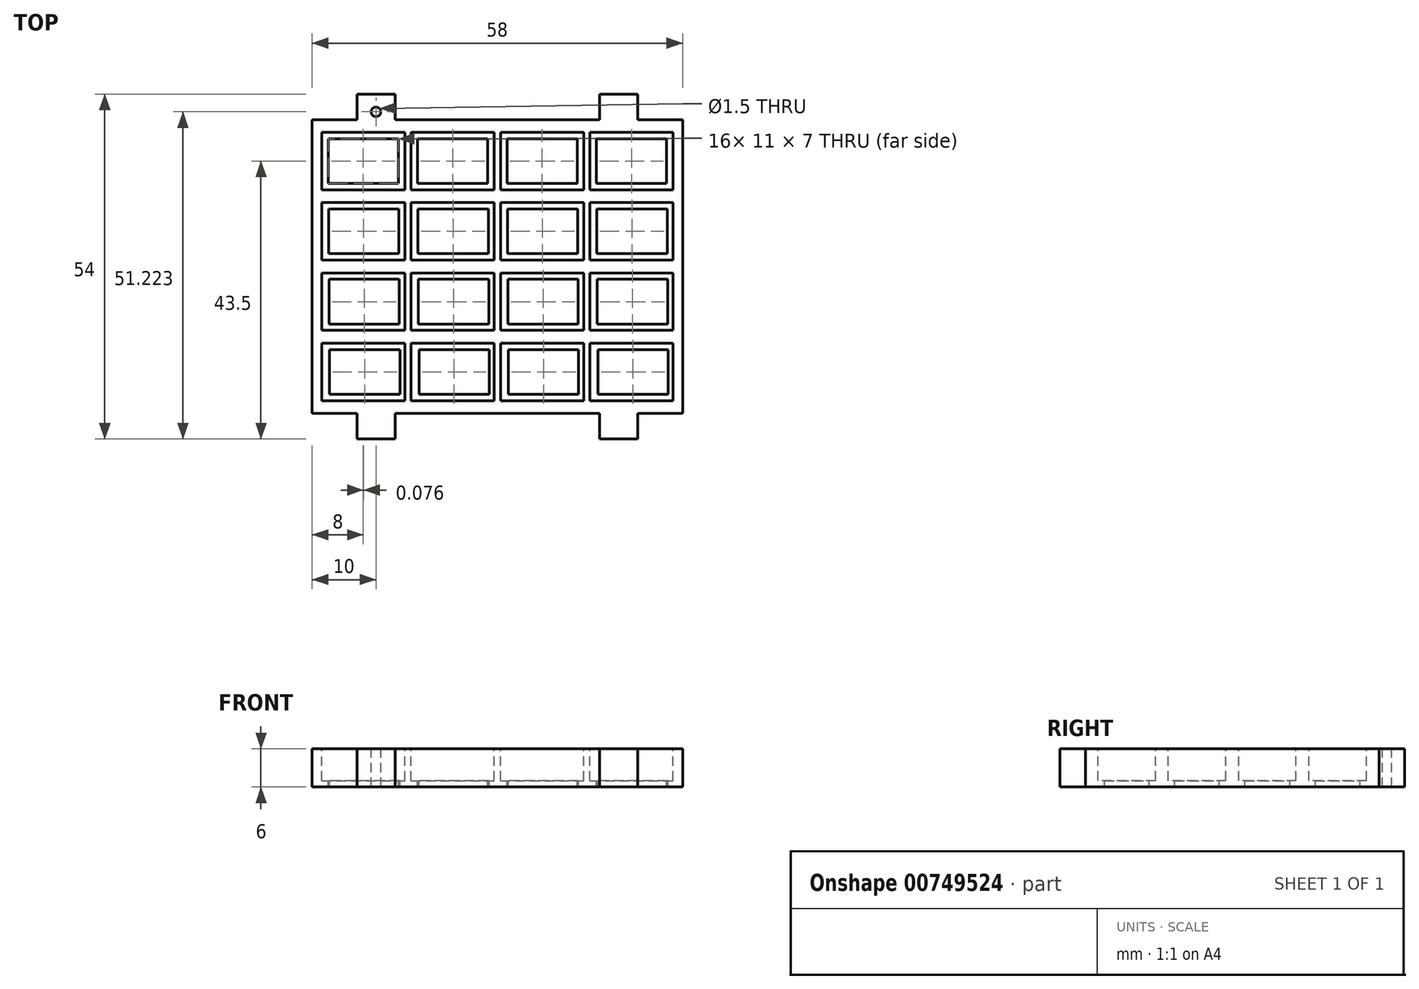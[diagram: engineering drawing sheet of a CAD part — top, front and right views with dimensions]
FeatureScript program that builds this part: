
annotation { "Feature Type Name" : "Feature", "Feature Type Description" : "" }
export const myFeature = defineFeature(function(context is Context, id is Id, definition is map)
    precondition{}
    {
        {
            var Q0;
            Q0=qCreatedBy(makeId("Top.planeOp"),FACE);
            var sketch = newSketch(context, id + "F0", { "sketchPlane" : qUnion([Q0])});
            skLineSegment(sketch, "E0.bottom", {"start": v(-29, 23) * mm, "end": v(29, 23) * mm});
            skLineSegment(sketch, "E0.top", {"start": v(-29, -23) * mm, "end": v(29, -23) * mm});
            skLineSegment(sketch, "E0.left", {"start": v(-29, 23) * mm, "end": v(-29, -23) * mm});
            skLineSegment(sketch, "E0.right", {"start": v(29, 23) * mm, "end": v(29, -23) * mm});
            skSolve(sketch);
        }
        {
            var Q0;
            Q0=makeQuery(id+"F0.imprint","IMPRINT",FACE,{"disambiguationData":[TD([[makeQuery(id+"F0.imprint","IMPRINT",EDGE,{"derivedFrom":sQuery(id+"F0.wireOp",EDGE,"E0.bottom")}),-1.0]])]});
            extrude(context, id + "F1", {"entities" : qUnion([Q0]), "depth" : 6 * mm, "offsetDistance" : 25 * mm});
        }
        {
            var Q0;
            Q0=makeQuery(id+"F1.opExtrude","CAP_FACE",FACE,{"disambiguationData":[OSD([sQuery(id+"F0.wireOp",EDGE,"E0.bottom"),sQuery(id+"F0.wireOp",EDGE,"E0.top"),sQuery(id+"F0.wireOp",EDGE,"E0.left"),sQuery(id+"F0.wireOp",EDGE,"E0.right")])],"isStart":false});
            var sketch = newSketch(context, id + "F2", { "sketchPlane" : qUnion([Q0])});
            skPoint(sketch, "E1.middle", {"position": v(0, 0) * mm});
            skLineSegment(sketch, "E2.bottom", {"start": v(-15.5, 13) * mm, "end": v(-26.5, 13) * mm});
            skLineSegment(sketch, "E2.top", {"start": v(-15.5, 20) * mm, "end": v(-26.5, 20) * mm});
            skLineSegment(sketch, "E2.left", {"start": v(-15.5, 13) * mm, "end": v(-15.5, 20) * mm});
            skLineSegment(sketch, "E2.right", {"start": v(-26.5, 13) * mm, "end": v(-26.5, 20) * mm});
            skPoint(sketch, "E2.middle", {"position": v(-21, 16.5) * mm});
            skLineSegment(sketch, "E3.1.0.0", {"start": v(-12.5, 13) * mm, "end": v(-12.5, 20) * mm});
            skLineSegment(sketch, "E3.1.0.1", {"start": v(-1.5, 13) * mm, "end": v(-1.5, 20) * mm});
            skLineSegment(sketch, "E3.1.0.2", {"start": v(-1.5, 20) * mm, "end": v(-12.5, 20) * mm});
            skPoint(sketch, "E3.1.0.3", {"position": v(-7, 16.5) * mm});
            skLineSegment(sketch, "E3.1.0.4", {"start": v(-1.5, 13) * mm, "end": v(-12.5, 13) * mm});
            skLineSegment(sketch, "E3.2.0.0", {"start": v(1.5, 13) * mm, "end": v(1.5, 20) * mm});
            skLineSegment(sketch, "E3.2.0.1", {"start": v(12.5, 13) * mm, "end": v(12.5, 20) * mm});
            skLineSegment(sketch, "E3.2.0.2", {"start": v(12.5, 20) * mm, "end": v(1.5, 20) * mm});
            skPoint(sketch, "E3.2.0.3", {"position": v(7, 16.5) * mm});
            skLineSegment(sketch, "E3.2.0.4", {"start": v(12.5, 13) * mm, "end": v(1.5, 13) * mm});
            skLineSegment(sketch, "E3.3.0.0", {"start": v(15.5, 13) * mm, "end": v(15.5, 20) * mm});
            skLineSegment(sketch, "E3.3.0.1", {"start": v(26.5, 13) * mm, "end": v(26.5, 20) * mm});
            skLineSegment(sketch, "E3.3.0.2", {"start": v(26.5, 20) * mm, "end": v(15.5, 20) * mm});
            skPoint(sketch, "E3.3.0.3", {"position": v(21, 16.5) * mm});
            skLineSegment(sketch, "E3.3.0.4", {"start": v(26.5, 13) * mm, "end": v(15.5, 13) * mm});
            skLineSegment(sketch, "E3.direction1", {"start": v(-26.5, 13) * mm, "end": v(-12.5, 13) * mm, "construction": true});
            skLineSegment(sketch, "E4.1.0.0", {"start": v(15.58, 2) * mm, "end": v(15.58, 9) * mm});
            skLineSegment(sketch, "E4.1.0.1", {"start": v(26.58, 9) * mm, "end": v(15.58, 9) * mm});
            skLineSegment(sketch, "E4.1.0.2", {"start": v(-26.42, 2) * mm, "end": v(-12.42, 2) * mm, "construction": true});
            skPoint(sketch, "E4.1.0.3", {"position": v(-20.92, 5.5) * mm});
            skLineSegment(sketch, "E4.1.0.4", {"start": v(1.58, 2) * mm, "end": v(1.58, 9) * mm});
            skLineSegment(sketch, "E4.1.0.5", {"start": v(-1.42, 2) * mm, "end": v(-12.42, 2) * mm});
            skLineSegment(sketch, "E4.1.0.6", {"start": v(-1.42, 9) * mm, "end": v(-12.42, 9) * mm});
            skLineSegment(sketch, "E4.1.0.7", {"start": v(-1.42, 2) * mm, "end": v(-1.42, 9) * mm});
            skLineSegment(sketch, "E4.1.0.8", {"start": v(-12.42, 2) * mm, "end": v(-12.42, 9) * mm});
            skLineSegment(sketch, "E4.1.0.9", {"start": v(-26.42, 2) * mm, "end": v(-26.42, 9) * mm});
            skLineSegment(sketch, "E4.1.0.10", {"start": v(-15.42, 2) * mm, "end": v(-15.42, 9) * mm});
            skLineSegment(sketch, "E4.1.0.11", {"start": v(-15.42, 9) * mm, "end": v(-26.42, 9) * mm});
            skPoint(sketch, "E4.1.0.12", {"position": v(7.08, 5.5) * mm});
            skLineSegment(sketch, "E4.1.0.13", {"start": v(12.58, 2) * mm, "end": v(1.58, 2) * mm});
            skLineSegment(sketch, "E4.1.0.14", {"start": v(12.58, 9) * mm, "end": v(1.58, 9) * mm});
            skLineSegment(sketch, "E4.1.0.15", {"start": v(12.58, 2) * mm, "end": v(12.58, 9) * mm});
            skLineSegment(sketch, "E4.1.0.16", {"start": v(26.58, 2) * mm, "end": v(26.58, 9) * mm});
            skLineSegment(sketch, "E4.1.0.17", {"start": v(26.58, 2) * mm, "end": v(15.58, 2) * mm});
            skPoint(sketch, "E4.1.0.18", {"position": v(-6.92, 5.5) * mm});
            skPoint(sketch, "E4.1.0.19", {"position": v(21.08, 5.5) * mm});
            skLineSegment(sketch, "E4.1.0.20", {"start": v(-15.42, 2) * mm, "end": v(-26.42, 2) * mm});
            skLineSegment(sketch, "E4.2.0.0", {"start": v(15.65, -9) * mm, "end": v(15.65, -2) * mm});
            skLineSegment(sketch, "E4.2.0.1", {"start": v(26.65, -2) * mm, "end": v(15.65, -2) * mm});
            skLineSegment(sketch, "E4.2.0.2", {"start": v(-26.35, -9) * mm, "end": v(-12.35, -9) * mm, "construction": true});
            skPoint(sketch, "E4.2.0.3", {"position": v(-20.85, -5.5) * mm});
            skLineSegment(sketch, "E4.2.0.4", {"start": v(1.65, -9) * mm, "end": v(1.65, -2) * mm});
            skLineSegment(sketch, "E4.2.0.5", {"start": v(-1.35, -9) * mm, "end": v(-12.35, -9) * mm});
            skLineSegment(sketch, "E4.2.0.6", {"start": v(-1.35, -2) * mm, "end": v(-12.35, -2) * mm});
            skLineSegment(sketch, "E4.2.0.7", {"start": v(-1.35, -9) * mm, "end": v(-1.35, -2) * mm});
            skLineSegment(sketch, "E4.2.0.8", {"start": v(-12.35, -9) * mm, "end": v(-12.35, -2) * mm});
            skLineSegment(sketch, "E4.2.0.9", {"start": v(-26.35, -9) * mm, "end": v(-26.35, -2) * mm});
            skLineSegment(sketch, "E4.2.0.10", {"start": v(-15.35, -9) * mm, "end": v(-15.35, -2) * mm});
            skLineSegment(sketch, "E4.2.0.11", {"start": v(-15.35, -2) * mm, "end": v(-26.35, -2) * mm});
            skPoint(sketch, "E4.2.0.12", {"position": v(7.15, -5.5) * mm});
            skLineSegment(sketch, "E4.2.0.13", {"start": v(12.65, -9) * mm, "end": v(1.65, -9) * mm});
            skLineSegment(sketch, "E4.2.0.14", {"start": v(12.65, -2) * mm, "end": v(1.65, -2) * mm});
            skLineSegment(sketch, "E4.2.0.15", {"start": v(12.65, -9) * mm, "end": v(12.65, -2) * mm});
            skLineSegment(sketch, "E4.2.0.16", {"start": v(26.65, -9) * mm, "end": v(26.65, -2) * mm});
            skLineSegment(sketch, "E4.2.0.17", {"start": v(26.65, -9) * mm, "end": v(15.65, -9) * mm});
            skPoint(sketch, "E4.2.0.18", {"position": v(-6.85, -5.5) * mm});
            skPoint(sketch, "E4.2.0.19", {"position": v(21.15, -5.5) * mm});
            skLineSegment(sketch, "E4.2.0.20", {"start": v(-15.35, -9) * mm, "end": v(-26.35, -9) * mm});
            skLineSegment(sketch, "E4.3.0.0", {"start": v(15.73, -20) * mm, "end": v(15.73, -13) * mm});
            skLineSegment(sketch, "E4.3.0.1", {"start": v(26.73, -13) * mm, "end": v(15.73, -13) * mm});
            skLineSegment(sketch, "E4.3.0.2", {"start": v(-26.27, -20) * mm, "end": v(-12.27, -20) * mm, "construction": true});
            skPoint(sketch, "E4.3.0.3", {"position": v(-20.77, -16.5) * mm});
            skLineSegment(sketch, "E4.3.0.4", {"start": v(1.73, -20) * mm, "end": v(1.73, -13) * mm});
            skLineSegment(sketch, "E4.3.0.5", {"start": v(-1.27, -20) * mm, "end": v(-12.27, -20) * mm});
            skLineSegment(sketch, "E4.3.0.6", {"start": v(-1.27, -13) * mm, "end": v(-12.27, -13) * mm});
            skLineSegment(sketch, "E4.3.0.7", {"start": v(-1.27, -20) * mm, "end": v(-1.27, -13) * mm});
            skLineSegment(sketch, "E4.3.0.8", {"start": v(-12.27, -20) * mm, "end": v(-12.27, -13) * mm});
            skLineSegment(sketch, "E4.3.0.9", {"start": v(-26.27, -20) * mm, "end": v(-26.27, -13) * mm});
            skLineSegment(sketch, "E4.3.0.10", {"start": v(-15.27, -20) * mm, "end": v(-15.27, -13) * mm});
            skLineSegment(sketch, "E4.3.0.11", {"start": v(-15.27, -13) * mm, "end": v(-26.27, -13) * mm});
            skPoint(sketch, "E4.3.0.12", {"position": v(7.23, -16.5) * mm});
            skLineSegment(sketch, "E4.3.0.13", {"start": v(12.73, -20) * mm, "end": v(1.73, -20) * mm});
            skLineSegment(sketch, "E4.3.0.14", {"start": v(12.73, -13) * mm, "end": v(1.73, -13) * mm});
            skLineSegment(sketch, "E4.3.0.15", {"start": v(12.73, -20) * mm, "end": v(12.73, -13) * mm});
            skLineSegment(sketch, "E4.3.0.16", {"start": v(26.73, -20) * mm, "end": v(26.73, -13) * mm});
            skLineSegment(sketch, "E4.3.0.17", {"start": v(26.73, -20) * mm, "end": v(15.73, -20) * mm});
            skPoint(sketch, "E4.3.0.18", {"position": v(-6.77, -16.5) * mm});
            skPoint(sketch, "E4.3.0.19", {"position": v(21.23, -16.5) * mm});
            skLineSegment(sketch, "E4.3.0.20", {"start": v(-15.27, -20) * mm, "end": v(-26.27, -20) * mm});
            skLineSegment(sketch, "E4.direction1", {"start": v(-26.5, 13) * mm, "end": v(-26.42, 2) * mm, "construction": true});
            skSolve(sketch);
        }
        {
            var Q0;
            Q0=makeQuery(id+"F2.imprint","IMPRINT",FACE,{"disambiguationData":[TD([[makeQuery(id+"F2.imprint","IMPRINT",EDGE,{"derivedFrom":sQuery(id+"F2.wireOp",EDGE,"E2.bottom")}),-1.0]])]});
            var Q1;
            Q1=makeQuery(id+"F2.imprint","IMPRINT",FACE,{"disambiguationData":[TD([[makeQuery(id+"F2.imprint","IMPRINT",EDGE,{"derivedFrom":sQuery(id+"F2.wireOp",EDGE,"E3.1.0.0")}),-1.0]])]});
            var Q2;
            Q2=makeQuery(id+"F2.imprint","IMPRINT",FACE,{"disambiguationData":[TD([[makeQuery(id+"F2.imprint","IMPRINT",EDGE,{"derivedFrom":sQuery(id+"F2.wireOp",EDGE,"E3.2.0.0")}),-1.0]])]});
            var Q3;
            Q3=makeQuery(id+"F2.imprint","IMPRINT",FACE,{"disambiguationData":[TD([[makeQuery(id+"F2.imprint","IMPRINT",EDGE,{"derivedFrom":sQuery(id+"F2.wireOp",EDGE,"E3.3.0.0")}),-1.0]])]});
            var Q4;
            Q4=makeQuery(id+"F2.imprint","IMPRINT",FACE,{"disambiguationData":[TD([[makeQuery(id+"F2.imprint","IMPRINT",EDGE,{"derivedFrom":sQuery(id+"F2.wireOp",EDGE,"E4.1.0.9")}),-1.0]])]});
            var Q5;
            Q5=makeQuery(id+"F2.imprint","IMPRINT",FACE,{"disambiguationData":[TD([[makeQuery(id+"F2.imprint","IMPRINT",EDGE,{"derivedFrom":sQuery(id+"F2.wireOp",EDGE,"E4.1.0.5")}),-1.0]])]});
            var Q6;
            Q6=makeQuery(id+"F2.imprint","IMPRINT",FACE,{"disambiguationData":[TD([[makeQuery(id+"F2.imprint","IMPRINT",EDGE,{"derivedFrom":sQuery(id+"F2.wireOp",EDGE,"E4.1.0.4")}),-1.0]])]});
            var Q7;
            Q7=makeQuery(id+"F2.imprint","IMPRINT",FACE,{"disambiguationData":[TD([[makeQuery(id+"F2.imprint","IMPRINT",EDGE,{"derivedFrom":sQuery(id+"F2.wireOp",EDGE,"E4.1.0.0")}),-1.0]])]});
            var Q8;
            Q8=makeQuery(id+"F2.imprint","IMPRINT",FACE,{"disambiguationData":[TD([[makeQuery(id+"F2.imprint","IMPRINT",EDGE,{"derivedFrom":sQuery(id+"F2.wireOp",EDGE,"E4.2.0.9")}),-1.0]])]});
            var Q9;
            Q9=makeQuery(id+"F2.imprint","IMPRINT",FACE,{"disambiguationData":[TD([[makeQuery(id+"F2.imprint","IMPRINT",EDGE,{"derivedFrom":sQuery(id+"F2.wireOp",EDGE,"E4.2.0.5")}),-1.0]])]});
            var Q10;
            Q10=makeQuery(id+"F2.imprint","IMPRINT",FACE,{"disambiguationData":[TD([[makeQuery(id+"F2.imprint","IMPRINT",EDGE,{"derivedFrom":sQuery(id+"F2.wireOp",EDGE,"E4.2.0.4")}),-1.0]])]});
            var Q11;
            Q11=makeQuery(id+"F2.imprint","IMPRINT",FACE,{"disambiguationData":[TD([[makeQuery(id+"F2.imprint","IMPRINT",EDGE,{"derivedFrom":sQuery(id+"F2.wireOp",EDGE,"E4.2.0.0")}),-1.0]])]});
            var Q12;
            Q12=makeQuery(id+"F2.imprint","IMPRINT",FACE,{"disambiguationData":[TD([[makeQuery(id+"F2.imprint","IMPRINT",EDGE,{"derivedFrom":sQuery(id+"F2.wireOp",EDGE,"E4.3.0.9")}),-1.0]])]});
            var Q13;
            Q13=makeQuery(id+"F2.imprint","IMPRINT",FACE,{"disambiguationData":[TD([[makeQuery(id+"F2.imprint","IMPRINT",EDGE,{"derivedFrom":sQuery(id+"F2.wireOp",EDGE,"E4.3.0.5")}),-1.0]])]});
            var Q14;
            Q14=makeQuery(id+"F2.imprint","IMPRINT",FACE,{"disambiguationData":[TD([[makeQuery(id+"F2.imprint","IMPRINT",EDGE,{"derivedFrom":sQuery(id+"F2.wireOp",EDGE,"E4.3.0.4")}),-1.0]])]});
            var Q15;
            Q15=makeQuery(id+"F2.imprint","IMPRINT",FACE,{"disambiguationData":[TD([[makeQuery(id+"F2.imprint","IMPRINT",EDGE,{"derivedFrom":sQuery(id+"F2.wireOp",EDGE,"E4.3.0.0")}),-1.0]])]});
            extrude(context, id + "F3", {"entities" : qUnion([Q0, Q1, Q2, Q3, Q4, Q5, Q6, Q7, Q8, Q9, Q10, Q11, Q12, Q13, Q14, Q15]), "operationType" : NewBodyOperationType.REMOVE, "endBound" : BoundingType.THROUGH_ALL, "oppositeDirection" : true, "depth" : 4 * mm, "offsetDistance" : 25 * mm});
        }
        {
            var Q0;
            Q0=makeQuery(id+"F1.opExtrude","CAP_FACE",FACE,{"disambiguationData":[OSD([sQuery(id+"F0.wireOp",EDGE,"E0.bottom"),sQuery(id+"F0.wireOp",EDGE,"E0.top"),sQuery(id+"F0.wireOp",EDGE,"E0.left"),sQuery(id+"F0.wireOp",EDGE,"E0.right")])],"isStart":false});
            var sketch = newSketch(context, id + "F4", { "sketchPlane" : qUnion([Q0])});
            skLineSegment(sketch, "E5.bottom", {"start": v(-27.5, 21) * mm, "end": v(-14.5, 21) * mm});
            skLineSegment(sketch, "E5.top", {"start": v(-27.5, 12) * mm, "end": v(-14.5, 12) * mm});
            skLineSegment(sketch, "E5.left", {"start": v(-27.5, 21) * mm, "end": v(-27.5, 12) * mm});
            skLineSegment(sketch, "E5.right", {"start": v(-14.5, 21) * mm, "end": v(-14.5, 12) * mm});
            skLineSegment(sketch, "E6.1.0.0", {"start": v(-13.5, 12) * mm, "end": v(-0.5, 12) * mm});
            skLineSegment(sketch, "E6.1.0.1", {"start": v(-13.5, 21) * mm, "end": v(-0.5, 21) * mm});
            skLineSegment(sketch, "E6.1.0.2", {"start": v(-13.5, 21) * mm, "end": v(-13.5, 12) * mm});
            skLineSegment(sketch, "E6.1.0.3", {"start": v(-0.5, 21) * mm, "end": v(-0.5, 12) * mm});
            skLineSegment(sketch, "E6.2.0.0", {"start": v(0.5, 12) * mm, "end": v(13.5, 12) * mm});
            skLineSegment(sketch, "E6.2.0.1", {"start": v(0.5, 21) * mm, "end": v(13.5, 21) * mm});
            skLineSegment(sketch, "E6.2.0.2", {"start": v(0.5, 21) * mm, "end": v(0.5, 12) * mm});
            skLineSegment(sketch, "E6.2.0.3", {"start": v(13.5, 21) * mm, "end": v(13.5, 12) * mm});
            skLineSegment(sketch, "E6.3.0.0", {"start": v(14.5, 12) * mm, "end": v(27.5, 12) * mm});
            skLineSegment(sketch, "E6.3.0.1", {"start": v(14.5, 21) * mm, "end": v(27.5, 21) * mm});
            skLineSegment(sketch, "E6.3.0.2", {"start": v(14.5, 21) * mm, "end": v(14.5, 12) * mm});
            skLineSegment(sketch, "E6.3.0.3", {"start": v(27.5, 21) * mm, "end": v(27.5, 12) * mm});
            skLineSegment(sketch, "E6.direction1", {"start": v(-27.5, 12) * mm, "end": v(-13.5, 12) * mm, "construction": true});
            skLineSegment(sketch, "E7.1.0.0", {"start": v(14.5, 1) * mm, "end": v(27.5, 1) * mm});
            skLineSegment(sketch, "E7.1.0.1", {"start": v(13.5, 10) * mm, "end": v(13.5, 1) * mm});
            skLineSegment(sketch, "E7.1.0.2", {"start": v(0.5, 10) * mm, "end": v(0.5, 1) * mm});
            skLineSegment(sketch, "E7.1.0.3", {"start": v(0.5, 10) * mm, "end": v(13.5, 10) * mm});
            skLineSegment(sketch, "E7.1.0.4", {"start": v(0.5, 1) * mm, "end": v(13.5, 1) * mm});
            skLineSegment(sketch, "E7.1.0.5", {"start": v(-0.5, 10) * mm, "end": v(-0.5, 1) * mm});
            skLineSegment(sketch, "E7.1.0.6", {"start": v(-13.5, 10) * mm, "end": v(-13.5, 1) * mm});
            skLineSegment(sketch, "E7.1.0.7", {"start": v(-13.5, 10) * mm, "end": v(-0.5, 10) * mm});
            skLineSegment(sketch, "E7.1.0.8", {"start": v(-14.5, 10) * mm, "end": v(-14.5, 1) * mm});
            skLineSegment(sketch, "E7.1.0.9", {"start": v(-27.5, 10) * mm, "end": v(-27.5, 1) * mm});
            skLineSegment(sketch, "E7.1.0.10", {"start": v(-27.5, 10) * mm, "end": v(-14.5, 10) * mm});
            skLineSegment(sketch, "E7.1.0.11", {"start": v(27.5, 10) * mm, "end": v(27.5, 1) * mm});
            skLineSegment(sketch, "E7.1.0.12", {"start": v(14.5, 10) * mm, "end": v(14.5, 1) * mm});
            skLineSegment(sketch, "E7.1.0.13", {"start": v(14.5, 10) * mm, "end": v(27.5, 10) * mm});
            skLineSegment(sketch, "E7.1.0.14", {"start": v(-27.5, 1) * mm, "end": v(-13.5, 1) * mm, "construction": true});
            skLineSegment(sketch, "E7.1.0.15", {"start": v(-27.5, 1) * mm, "end": v(-14.5, 1) * mm});
            skLineSegment(sketch, "E7.1.0.16", {"start": v(-13.5, 1) * mm, "end": v(-0.5, 1) * mm});
            skLineSegment(sketch, "E7.2.0.0", {"start": v(14.5, -10) * mm, "end": v(27.5, -10) * mm});
            skLineSegment(sketch, "E7.2.0.1", {"start": v(13.5, -1) * mm, "end": v(13.5, -10) * mm});
            skLineSegment(sketch, "E7.2.0.2", {"start": v(0.5, -1) * mm, "end": v(0.5, -10) * mm});
            skLineSegment(sketch, "E7.2.0.3", {"start": v(0.5, -1) * mm, "end": v(13.5, -1) * mm});
            skLineSegment(sketch, "E7.2.0.4", {"start": v(0.5, -10) * mm, "end": v(13.5, -10) * mm});
            skLineSegment(sketch, "E7.2.0.5", {"start": v(-0.5, -1) * mm, "end": v(-0.5, -10) * mm});
            skLineSegment(sketch, "E7.2.0.6", {"start": v(-13.5, -1) * mm, "end": v(-13.5, -10) * mm});
            skLineSegment(sketch, "E7.2.0.7", {"start": v(-13.5, -1) * mm, "end": v(-0.5, -1) * mm});
            skLineSegment(sketch, "E7.2.0.8", {"start": v(-14.5, -1) * mm, "end": v(-14.5, -10) * mm});
            skLineSegment(sketch, "E7.2.0.9", {"start": v(-27.5, -1) * mm, "end": v(-27.5, -10) * mm});
            skLineSegment(sketch, "E7.2.0.10", {"start": v(-27.5, -1) * mm, "end": v(-14.5, -1) * mm});
            skLineSegment(sketch, "E7.2.0.11", {"start": v(27.5, -1) * mm, "end": v(27.5, -10) * mm});
            skLineSegment(sketch, "E7.2.0.12", {"start": v(14.5, -1) * mm, "end": v(14.5, -10) * mm});
            skLineSegment(sketch, "E7.2.0.13", {"start": v(14.5, -1) * mm, "end": v(27.5, -1) * mm});
            skLineSegment(sketch, "E7.2.0.14", {"start": v(-27.5, -10) * mm, "end": v(-13.5, -10) * mm, "construction": true});
            skLineSegment(sketch, "E7.2.0.15", {"start": v(-27.5, -10) * mm, "end": v(-14.5, -10) * mm});
            skLineSegment(sketch, "E7.2.0.16", {"start": v(-13.5, -10) * mm, "end": v(-0.5, -10) * mm});
            skLineSegment(sketch, "E7.3.0.0", {"start": v(14.5, -21) * mm, "end": v(27.5, -21) * mm});
            skLineSegment(sketch, "E7.3.0.1", {"start": v(13.5, -12) * mm, "end": v(13.5, -21) * mm});
            skLineSegment(sketch, "E7.3.0.2", {"start": v(0.5, -12) * mm, "end": v(0.5, -21) * mm});
            skLineSegment(sketch, "E7.3.0.3", {"start": v(0.5, -12) * mm, "end": v(13.5, -12) * mm});
            skLineSegment(sketch, "E7.3.0.4", {"start": v(0.5, -21) * mm, "end": v(13.5, -21) * mm});
            skLineSegment(sketch, "E7.3.0.5", {"start": v(-0.5, -12) * mm, "end": v(-0.5, -21) * mm});
            skLineSegment(sketch, "E7.3.0.6", {"start": v(-13.5, -12) * mm, "end": v(-13.5, -21) * mm});
            skLineSegment(sketch, "E7.3.0.7", {"start": v(-13.5, -12) * mm, "end": v(-0.5, -12) * mm});
            skLineSegment(sketch, "E7.3.0.8", {"start": v(-14.5, -12) * mm, "end": v(-14.5, -21) * mm});
            skLineSegment(sketch, "E7.3.0.9", {"start": v(-27.5, -12) * mm, "end": v(-27.5, -21) * mm});
            skLineSegment(sketch, "E7.3.0.10", {"start": v(-27.5, -12) * mm, "end": v(-14.5, -12) * mm});
            skLineSegment(sketch, "E7.3.0.11", {"start": v(27.5, -12) * mm, "end": v(27.5, -21) * mm});
            skLineSegment(sketch, "E7.3.0.12", {"start": v(14.5, -12) * mm, "end": v(14.5, -21) * mm});
            skLineSegment(sketch, "E7.3.0.13", {"start": v(14.5, -12) * mm, "end": v(27.5, -12) * mm});
            skLineSegment(sketch, "E7.3.0.14", {"start": v(-27.5, -21) * mm, "end": v(-13.5, -21) * mm, "construction": true});
            skLineSegment(sketch, "E7.3.0.15", {"start": v(-27.5, -21) * mm, "end": v(-14.5, -21) * mm});
            skLineSegment(sketch, "E7.3.0.16", {"start": v(-13.5, -21) * mm, "end": v(-0.5, -21) * mm});
            skLineSegment(sketch, "E7.direction1", {"start": v(-27.5, 12) * mm, "end": v(-27.5, 1) * mm, "construction": true});
            skSolve(sketch);
        }
        {
            var Q0;
            Q0=makeQuery(id+"F4.imprint","IMPRINT",FACE,{"disambiguationData":[TD([[makeQuery(id+"F4.imprint","IMPRINT",EDGE,{"derivedFrom":sQuery(id+"F4.wireOp",EDGE,"E5.bottom")}),-1.0]])]});
            var Q1;
            Q1=makeQuery(id+"F4.imprint","IMPRINT",FACE,{"disambiguationData":[TD([[makeQuery(id+"F4.imprint","IMPRINT",EDGE,{"derivedFrom":sQuery(id+"F4.wireOp",EDGE,"E6.1.0.0")}),1.0]])]});
            var Q2;
            Q2=makeQuery(id+"F4.imprint","IMPRINT",FACE,{"disambiguationData":[TD([[makeQuery(id+"F4.imprint","IMPRINT",EDGE,{"derivedFrom":sQuery(id+"F4.wireOp",EDGE,"E6.2.0.0")}),1.0]])]});
            var Q3;
            Q3=makeQuery(id+"F4.imprint","IMPRINT",FACE,{"disambiguationData":[TD([[makeQuery(id+"F4.imprint","IMPRINT",EDGE,{"derivedFrom":sQuery(id+"F4.wireOp",EDGE,"E6.3.0.0")}),1.0]])]});
            var Q4;
            Q4=makeQuery(id+"F4.imprint","IMPRINT",FACE,{"disambiguationData":[TD([[makeQuery(id+"F4.imprint","IMPRINT",EDGE,{"derivedFrom":sQuery(id+"F4.wireOp",EDGE,"E7.1.0.8")}),-1.0]])]});
            var Q5;
            Q5=makeQuery(id+"F4.imprint","IMPRINT",FACE,{"disambiguationData":[TD([[makeQuery(id+"F4.imprint","IMPRINT",EDGE,{"derivedFrom":sQuery(id+"F4.wireOp",EDGE,"E7.1.0.1")}),-1.0]])]});
            var Q6;
            Q6=makeQuery(id+"F4.imprint","IMPRINT",FACE,{"disambiguationData":[TD([[makeQuery(id+"F4.imprint","IMPRINT",EDGE,{"derivedFrom":sQuery(id+"F4.wireOp",EDGE,"E7.1.0.5")}),-1.0]])]});
            var Q7;
            Q7=makeQuery(id+"F4.imprint","IMPRINT",FACE,{"disambiguationData":[TD([[makeQuery(id+"F4.imprint","IMPRINT",EDGE,{"derivedFrom":sQuery(id+"F4.wireOp",EDGE,"E7.1.0.0")}),1.0]])]});
            var Q8;
            Q8=makeQuery(id+"F4.imprint","IMPRINT",FACE,{"disambiguationData":[TD([[makeQuery(id+"F4.imprint","IMPRINT",EDGE,{"derivedFrom":sQuery(id+"F4.wireOp",EDGE,"E7.2.0.8")}),-1.0]])]});
            var Q9;
            Q9=makeQuery(id+"F4.imprint","IMPRINT",FACE,{"disambiguationData":[TD([[makeQuery(id+"F4.imprint","IMPRINT",EDGE,{"derivedFrom":sQuery(id+"F4.wireOp",EDGE,"E7.2.0.5")}),-1.0]])]});
            var Q10;
            Q10=makeQuery(id+"F4.imprint","IMPRINT",FACE,{"disambiguationData":[TD([[makeQuery(id+"F4.imprint","IMPRINT",EDGE,{"derivedFrom":sQuery(id+"F4.wireOp",EDGE,"E7.2.0.1")}),-1.0]])]});
            var Q11;
            Q11=makeQuery(id+"F4.imprint","IMPRINT",FACE,{"disambiguationData":[TD([[makeQuery(id+"F4.imprint","IMPRINT",EDGE,{"derivedFrom":sQuery(id+"F4.wireOp",EDGE,"E7.2.0.0")}),1.0]])]});
            var Q12;
            Q12=makeQuery(id+"F4.imprint","IMPRINT",FACE,{"disambiguationData":[TD([[makeQuery(id+"F4.imprint","IMPRINT",EDGE,{"derivedFrom":sQuery(id+"F4.wireOp",EDGE,"E7.3.0.8")}),-1.0]])]});
            var Q13;
            Q13=makeQuery(id+"F4.imprint","IMPRINT",FACE,{"disambiguationData":[TD([[makeQuery(id+"F4.imprint","IMPRINT",EDGE,{"derivedFrom":sQuery(id+"F4.wireOp",EDGE,"E7.3.0.5")}),-1.0]])]});
            var Q14;
            Q14=makeQuery(id+"F4.imprint","IMPRINT",FACE,{"disambiguationData":[TD([[makeQuery(id+"F4.imprint","IMPRINT",EDGE,{"derivedFrom":sQuery(id+"F4.wireOp",EDGE,"E7.3.0.1")}),-1.0]])]});
            var Q15;
            Q15=makeQuery(id+"F4.imprint","IMPRINT",FACE,{"disambiguationData":[TD([[makeQuery(id+"F4.imprint","IMPRINT",EDGE,{"derivedFrom":sQuery(id+"F4.wireOp",EDGE,"E7.3.0.0")}),1.0]])]});
            extrude(context, id + "F5", {"entities" : qUnion([Q0, Q1, Q2, Q3, Q4, Q5, Q6, Q7, Q8, Q9, Q10, Q11, Q12, Q13, Q14, Q15]), "operationType" : NewBodyOperationType.REMOVE, "oppositeDirection" : true, "depth" : 5 * mm, "offsetDistance" : 25 * mm});
        }
        {
            var Q0;
            Q0=makeQuery(id+"F1.opExtrude","SWEPT_FACE",FACE,{"disambiguationData":[OSD([sQuery(id+"F0.wireOp",EDGE,"E0.bottom")])]});
            var sketch = newSketch(context, id + "F6", { "sketchPlane" : qUnion([Q0])});
            skLineSegment(sketch, "E8.bottom", {"start": v(22, 0) * mm, "end": v(16, 0) * mm});
            skLineSegment(sketch, "E8.top", {"start": v(22, 6) * mm, "end": v(16, 6) * mm});
            skLineSegment(sketch, "E8.left", {"start": v(22, 0) * mm, "end": v(22, 6) * mm});
            skLineSegment(sketch, "E8.right", {"start": v(16, 0) * mm, "end": v(16, 6) * mm});
            skLineSegment(sketch, "E9.bottom", {"start": v(-16, 0) * mm, "end": v(-22, 0) * mm});
            skLineSegment(sketch, "E9.top", {"start": v(-16, 6) * mm, "end": v(-22, 6) * mm});
            skLineSegment(sketch, "E9.left", {"start": v(-16, 0) * mm, "end": v(-16, 6) * mm});
            skLineSegment(sketch, "E9.right", {"start": v(-22, 0) * mm, "end": v(-22, 6) * mm});
            skSolve(sketch);
        }
        {
            var Q0;
            Q0=makeQuery(id+"F6.imprint","IMPRINT",FACE,{"disambiguationData":[TD([[makeQuery(id+"F6.imprint","IMPRINT",EDGE,{"derivedFrom":sQuery(id+"F6.wireOp",EDGE,"E8.bottom")}),-1.0]])]});
            var Q1;
            Q1=makeQuery(id+"F6.imprint","IMPRINT",FACE,{"disambiguationData":[TD([[makeQuery(id+"F6.imprint","IMPRINT",EDGE,{"derivedFrom":sQuery(id+"F6.wireOp",EDGE,"E9.bottom")}),-1.0]])]});
            extrude(context, id + "F7", {"entities" : qUnion([Q0, Q1]), "operationType" : NewBodyOperationType.ADD, "depth" : 4 * mm, "offsetDistance" : 25 * mm});
        }
        {
            var Q0;
            Q0=makeQuery(id+"F1.opExtrude","SWEPT_FACE",FACE,{"disambiguationData":[OSD([sQuery(id+"F0.wireOp",EDGE,"E0.top")])]});
            var sketch = newSketch(context, id + "F8", { "sketchPlane" : qUnion([Q0])});
            skLineSegment(sketch, "E10.bottom", {"start": v(22, 0) * mm, "end": v(16, 0) * mm});
            skLineSegment(sketch, "E10.top", {"start": v(22, 6) * mm, "end": v(16, 6) * mm});
            skLineSegment(sketch, "E10.left", {"start": v(22, 0) * mm, "end": v(22, 6) * mm});
            skLineSegment(sketch, "E10.right", {"start": v(16, 0) * mm, "end": v(16, 6) * mm});
            skLineSegment(sketch, "E11.bottom", {"start": v(-16, 0) * mm, "end": v(-22, 0) * mm});
            skLineSegment(sketch, "E11.top", {"start": v(-16, 6) * mm, "end": v(-22, 6) * mm});
            skLineSegment(sketch, "E11.left", {"start": v(-16, 0) * mm, "end": v(-16, 6) * mm});
            skLineSegment(sketch, "E11.right", {"start": v(-22, 0) * mm, "end": v(-22, 6) * mm});
            skSolve(sketch);
        }
        {
            var Q0;
            Q0=makeQuery(id+"F8.imprint","IMPRINT",FACE,{"disambiguationData":[TD([[makeQuery(id+"F8.imprint","IMPRINT",EDGE,{"derivedFrom":sQuery(id+"F8.wireOp",EDGE,"E10.bottom")}),1.0]])]});
            var Q1;
            Q1=makeQuery(id+"F8.imprint","IMPRINT",FACE,{"disambiguationData":[TD([[makeQuery(id+"F8.imprint","IMPRINT",EDGE,{"derivedFrom":sQuery(id+"F8.wireOp",EDGE,"E11.bottom")}),1.0]])]});
            extrude(context, id + "F9", {"entities" : qUnion([Q0, Q1]), "operationType" : NewBodyOperationType.ADD, "depth" : 4 * mm, "offsetDistance" : 25 * mm});
        }
        {
            var Q0;
            Q0=makeQuery(id+"F9.boolean.opBoolean","MERGE",FACE,{"derivedFrom":[makeQuery(id+"F7.boolean.opBoolean","MERGE",FACE,{"derivedFrom":[makeQuery(id+"F1.opExtrude","CAP_FACE",FACE,{"disambiguationData":[OSD([sQuery(id+"F0.wireOp",EDGE,"E0.bottom"),sQuery(id+"F0.wireOp",EDGE,"E0.top"),sQuery(id+"F0.wireOp",EDGE,"E0.left"),sQuery(id+"F0.wireOp",EDGE,"E0.right")])],"isStart":false}),makeQuery(id+"F7.opExtrude","SWEPT_FACE",FACE,{"disambiguationData":[OSD([sQuery(id+"F6.wireOp",EDGE,"E8.top")])]}),makeQuery(id+"F7.opExtrude","SWEPT_FACE",FACE,{"disambiguationData":[OSD([sQuery(id+"F6.wireOp",EDGE,"E9.top")])]})]}),makeQuery(id+"F9.opExtrude","SWEPT_FACE",FACE,{"disambiguationData":[OSD([sQuery(id+"F8.wireOp",EDGE,"E10.top")])]}),makeQuery(id+"F9.opExtrude","SWEPT_FACE",FACE,{"disambiguationData":[OSD([sQuery(id+"F8.wireOp",EDGE,"E11.top")])]})]});
            var sketch = newSketch(context, id + "F10", { "sketchPlane" : qUnion([Q0])});
            skCircle(sketch, "E12", {"center": v(-19, 24.22) * mm, "radius": 0.75 * mm});
            skPoint(sketch, "E12.centerSnap0", {"position": v(-19, 27) * mm});
            skSolve(sketch);
        }
        {
            var Q0;
            Q0=makeQuery(id+"F10.imprint","IMPRINT",FACE,{"disambiguationData":[TD([[makeQuery(id+"F10.imprint","IMPRINT",EDGE,{"derivedFrom":sQuery(id+"F10.wireOp",EDGE,"E12")}),1.0]])]});
            extrude(context, id + "F11", {"entities" : qUnion([Q0]), "operationType" : NewBodyOperationType.REMOVE, "endBound" : BoundingType.THROUGH_ALL, "oppositeDirection" : true, "depth" : 25 * mm, "offsetDistance" : 25 * mm});
        }
    });
